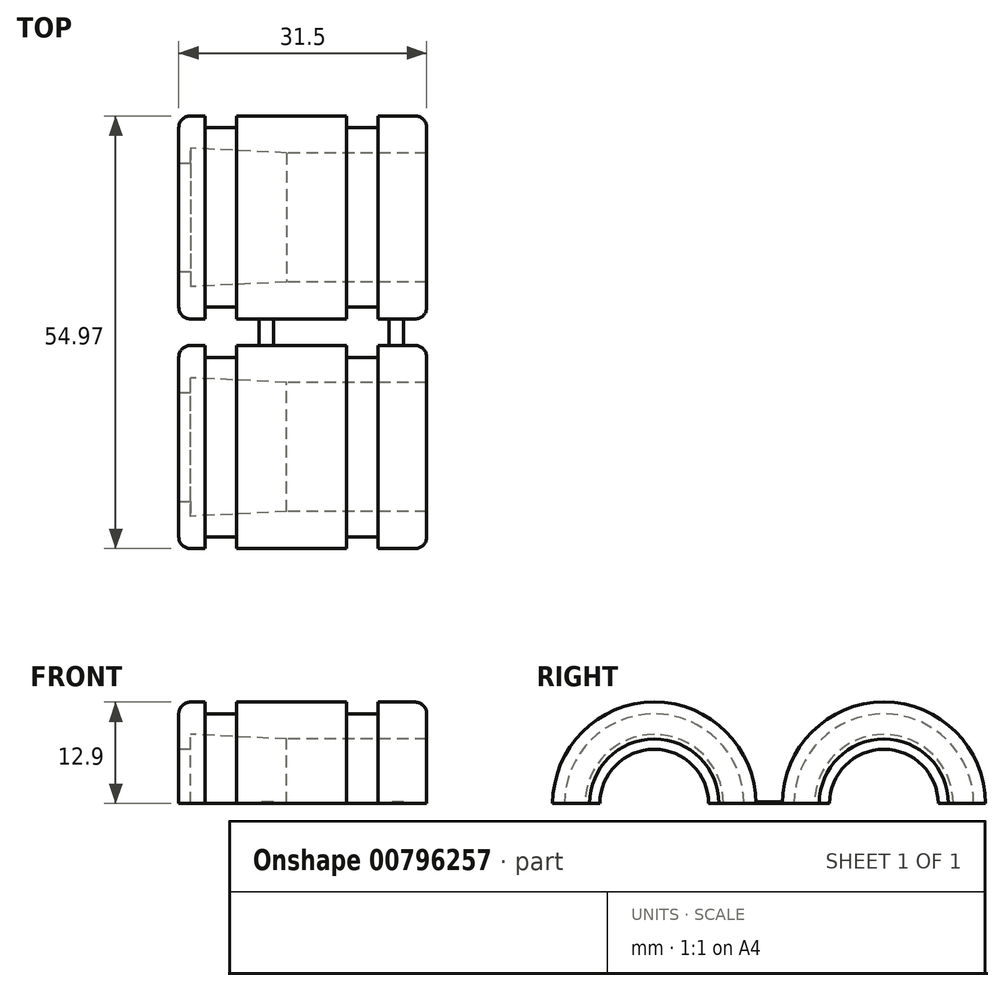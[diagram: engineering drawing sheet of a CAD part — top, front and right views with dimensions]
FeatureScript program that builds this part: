
annotation { "Feature Type Name" : "Feature", "Feature Type Description" : "" }
export const myFeature = defineFeature(function(context is Context, id is Id, definition is map)
    precondition{}
    {
        {
            var Q0;
            Q0=qCreatedBy(makeId("Top.planeOp"),FACE);
            var sketch = newSketch(context, id + "F0", { "sketchPlane" : qUnion([Q0])});
            skLineSegment(sketch, "E0", {"start": v(0, 0) * mm, "end": v(0, 8.8) * mm, "construction": true});
            skLineSegment(sketch, "E1", {"start": v(0, 0) * mm, "end": v(30, 0) * mm, "construction": true});
            skLineSegment(sketch, "E2", {"start": v(30, 0) * mm, "end": v(30, 8.2) * mm, "construction": true});
            skLineSegment(sketch, "E3", {"start": v(12.21, 0) * mm, "end": v(12.21, 8.2) * mm, "construction": true});
            skLineSegment(sketch, "E4", {"start": v(30, 0) * mm, "end": v(30, 12.9) * mm, "construction": true});
            skLineSegment(sketch, "E5", {"start": v(28.5, 12.9) * mm, "end": v(23.8, 12.9) * mm});
            skLineSegment(sketch, "E6", {"start": v(30, 11.4) * mm, "end": v(30, 8.2) * mm});
            skLineSegment(sketch, "E7", {"start": v(30, 8.2) * mm, "end": v(12.21, 8.2) * mm});
            skLineSegment(sketch, "E8", {"start": v(12.21, 8.2) * mm, "end": v(0, 8.8) * mm});
            skLineSegment(sketch, "E9.trimOffspring", {"start": v(19.8, 12.9) * mm, "end": v(5.84, 12.9) * mm});
            skLineSegment(sketch, "E10.trimOffspring", {"start": v(1.84, 12.9) * mm, "end": v(0, 12.9) * mm});
            skLineSegment(sketch, "E11", {"start": v(5.84, 12.9) * mm, "end": v(5.84, 11.4) * mm});
            skLineSegment(sketch, "E12", {"start": v(5.84, 11.4) * mm, "end": v(1.84, 11.4) * mm});
            skLineSegment(sketch, "E13", {"start": v(1.84, 11.4) * mm, "end": v(1.84, 12.9) * mm});
            skLineSegment(sketch, "E14", {"start": v(19.8, 12.9) * mm, "end": v(19.8, 11.4) * mm});
            skLineSegment(sketch, "E15", {"start": v(19.8, 11.4) * mm, "end": v(23.8, 11.4) * mm});
            skLineSegment(sketch, "E16", {"start": v(23.8, 11.4) * mm, "end": v(23.8, 12.9) * mm});
            skLineSegment(sketch, "E17", {"start": v(0, 12.9) * mm, "end": v(0, 12.9) * mm});
            skLineSegment(sketch, "E18", {"start": v(-1.5, 11.4) * mm, "end": v(-1.5, 6.9) * mm});
            skLineSegment(sketch, "E19", {"start": v(-1.5, 6.9) * mm, "end": v(0, 6.9) * mm});
            skLineSegment(sketch, "E20", {"start": v(0, 6.9) * mm, "end": v(0, 8.8) * mm});
            skPoint(sketch, "E21.visualSharp", {"position": v(30, 12.9) * mm});
            skArc(sketch, "E21.filletArc", {"start": v(30, 11.4) * mm, "mid": v(29.56, 12.46) * mm, "end": v(28.5, 12.9) * mm});
            skPoint(sketch, "E22.visualSharp", {"position": v(-1.5, 12.9) * mm});
            skArc(sketch, "E22.filletArc", {"start": v(0, 12.9) * mm, "mid": v(-1.06, 12.46) * mm, "end": v(-1.5, 11.4) * mm});
            skLineSegment(sketch, "E23", {"start": v(33.77, 14.58) * mm, "end": v(-4.52, 14.58) * mm, "construction": true});
            skLineSegment(sketch, "E24.MirrorCS", {"start": v(23.8, 17.77) * mm, "end": v(23.8, 16.27) * mm});
            skArc(sketch, "E25.MirrorCS", {"start": v(30, 17.77) * mm, "mid": v(29.56, 16.7) * mm, "end": v(28.5, 16.27) * mm});
            skLineSegment(sketch, "E26.MirrorCS", {"start": v(5.84, 16.27) * mm, "end": v(5.84, 17.77) * mm});
            skLineSegment(sketch, "E27.MirrorCS", {"start": v(1.84, 17.77) * mm, "end": v(1.84, 16.27) * mm});
            skLineSegment(sketch, "E28.MirrorCS", {"start": v(-1.5, 22.27) * mm, "end": v(0, 22.27) * mm});
            skLineSegment(sketch, "E29.MirrorCS", {"start": v(0, 22.27) * mm, "end": v(0, 20.37) * mm});
            skArc(sketch, "E30.MirrorCS", {"start": v(0, 16.27) * mm, "mid": v(-1.06, 16.7) * mm, "end": v(-1.5, 17.77) * mm});
            skLineSegment(sketch, "E31.MirrorCS", {"start": v(1.84, 16.27) * mm, "end": v(0, 16.27) * mm});
            skLineSegment(sketch, "E32.MirrorCS", {"start": v(19.8, 16.27) * mm, "end": v(19.8, 17.77) * mm});
            skLineSegment(sketch, "E33.MirrorCS", {"start": v(19.8, 17.77) * mm, "end": v(23.8, 17.77) * mm});
            skLineSegment(sketch, "E34.MirrorCS", {"start": v(30, 17.77) * mm, "end": v(30, 20.97) * mm});
            skLineSegment(sketch, "E35.MirrorCS", {"start": v(28.5, 16.27) * mm, "end": v(23.8, 16.27) * mm});
            skLineSegment(sketch, "E36.MirrorCS", {"start": v(30, 20.97) * mm, "end": v(12.21, 20.97) * mm});
            skPoint(sketch, "E37.MirrorP", {"position": v(30, 16.27) * mm});
            skLineSegment(sketch, "E38.MirrorCS", {"start": v(-1.5, 17.77) * mm, "end": v(-1.5, 22.27) * mm});
            skLineSegment(sketch, "E39.MirrorCS", {"start": v(0, 16.27) * mm, "end": v(0, 16.27) * mm});
            skLineSegment(sketch, "E40.MirrorCS", {"start": v(12.21, 20.97) * mm, "end": v(0, 20.37) * mm});
            skPoint(sketch, "E41.MirrorP", {"position": v(-1.5, 16.27) * mm});
            skLineSegment(sketch, "E42.MirrorCS", {"start": v(19.8, 16.27) * mm, "end": v(5.84, 16.27) * mm});
            skLineSegment(sketch, "E43.MirrorCS", {"start": v(5.84, 17.77) * mm, "end": v(1.84, 17.77) * mm});
            skLineSegment(sketch, "E44.MirrorCS", {"start": v(0, 29.17) * mm, "end": v(30, 29.17) * mm, "construction": true});
            skSolve(sketch);
        }
        {
            var Q0;
            Q0=qCreatedBy(makeId("Top.planeOp"),FACE);
            var sketch = newSketch(context, id + "F1", { "sketchPlane" : qUnion([Q0])});
            skLineSegment(sketch, "E45.bottom", {"start": v(27.06, 12.65) * mm, "end": v(25.23, 12.65) * mm});
            skLineSegment(sketch, "E45.top", {"start": v(27.06, 16.7) * mm, "end": v(25.23, 16.7) * mm});
            skLineSegment(sketch, "E45.left", {"start": v(27.06, 12.65) * mm, "end": v(27.06, 16.7) * mm});
            skLineSegment(sketch, "E45.right", {"start": v(25.23, 12.65) * mm, "end": v(25.23, 16.7) * mm});
            skLineSegment(sketch, "E46.bottom", {"start": v(8.7, 12.65) * mm, "end": v(10.53, 12.65) * mm});
            skLineSegment(sketch, "E46.top", {"start": v(8.7, 16.7) * mm, "end": v(10.53, 16.7) * mm});
            skLineSegment(sketch, "E46.left", {"start": v(8.7, 12.65) * mm, "end": v(8.7, 16.7) * mm});
            skLineSegment(sketch, "E46.right", {"start": v(10.53, 12.65) * mm, "end": v(10.53, 16.7) * mm});
            skSolve(sketch);
        }
        {
            var Q0;
            Q0=makeQuery(id+"F0.imprint","IMPRINT",FACE,{"disambiguationData":[TD([[makeQuery(id+"F0.imprint","IMPRINT",EDGE,{"derivedFrom":sQuery(id+"F0.wireOp",EDGE,"E5")}),1.0]])]});
            var Q1;
            Q1=sQuery(id+"F0.wireOp",EDGE,"E1");
            revolve(context, id + "F2", {"surfaceOperationType" : NewSurfaceOperationType.NEW, "entities" : qUnion([Q0]), "axis" : qUnion([Q1]), "revolveType" : RevolveType.ONE_DIRECTION, "angle" : 180 * degree});
        }
        {
            var Q0;
            Q0=makeQuery(id+"F0.imprint","IMPRINT",FACE,{"disambiguationData":[TD([[makeQuery(id+"F0.imprint","IMPRINT",EDGE,{"derivedFrom":sQuery(id+"F0.wireOp",EDGE,"E24.MirrorCS")}),1.0]])]});
            var Q1;
            Q1=sQuery(id+"F0.wireOp",EDGE,"E44.MirrorCS");
            revolve(context, id + "F3", {"surfaceOperationType" : NewSurfaceOperationType.NEW, "entities" : qUnion([Q0]), "axis" : qUnion([Q1]), "revolveType" : RevolveType.ONE_DIRECTION, "oppositeDirection" : true, "angle" : 180 * degree});
        }
        {
            var Q0;
            Q0=makeQuery(id+"F1.imprint","IMPRINT",FACE,{"disambiguationData":[TD([[makeQuery(id+"F1.imprint","IMPRINT",EDGE,{"derivedFrom":sQuery(id+"F1.wireOp",EDGE,"E45.bottom")}),-1.0]])]});
            var Q1;
            Q1=makeQuery(id+"F1.imprint","IMPRINT",FACE,{"disambiguationData":[TD([[makeQuery(id+"F1.imprint","IMPRINT",EDGE,{"derivedFrom":sQuery(id+"F1.wireOp",EDGE,"E46.bottom")}),1.0]])]});
            extrude(context, id + "F4", {"entities" : qUnion([Q0, Q1]), "operationType" : NewBodyOperationType.ADD, "depth" : 0.25 * mm, "offsetDistance" : 25 * mm});
        }
    });
